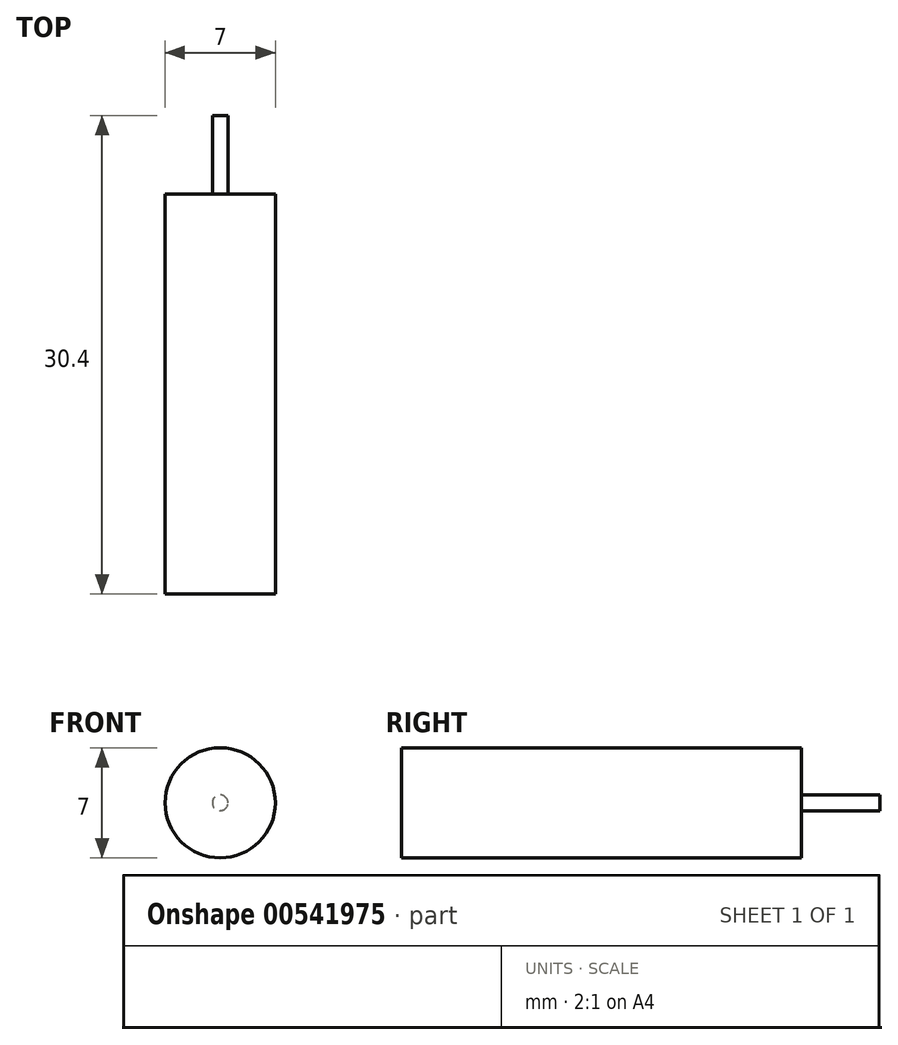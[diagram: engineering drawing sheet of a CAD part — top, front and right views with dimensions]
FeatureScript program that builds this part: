
annotation { "Feature Type Name" : "Feature", "Feature Type Description" : "" }
export const myFeature = defineFeature(function(context is Context, id is Id, definition is map)
    precondition{}
    {
        {
            var Q0;
            Q0=qCreatedBy(makeId("Front.planeOp"),FACE);
            var sketch = newSketch(context, id + "F0", { "sketchPlane" : qUnion([Q0])});
            skCircle(sketch, "E0", {"center": v(0, 0) * mm, "radius": 3.5 * mm});
            skSolve(sketch);
        }
        {
            var Q0;
            Q0 = qSketchRegion(id + "F0", true);
            var sketch = newSketch(context, id + "F1", { "sketchPlane" : qUnion([Q0])});
            skSolve(sketch);
        }
        {
            var Q0;
            Q0 = qSketchRegion(id + "F1", true);
            var Q1;
            Q1=makeQuery(id+"F1.imprint","IMPRINT",FACE,{"disambiguationData":[TD([[makeQuery(id+"F1.imprint","IMPRINT",EDGE,{"derivedFrom":makeQuery(id+"F0.imprint","IMPRINT",EDGE,{"derivedFrom":sQuery(id+"F0.wireOp",EDGE,"E0")})}),1.0]])]});
            extrude(context, id + "F2", {"entities" : qUnion([Q0, Q1]), "depth" : 15 * mm, "offsetDistance" : 25.4 * mm});
        }
        {
            var Q0;
            Q0 = qSketchRegion(id + "F0", true);
            var sketch = newSketch(context, id + "F3", { "sketchPlane" : qUnion([Q0])});
            skCircle(sketch, "E1", {"center": v(0, 0) * mm, "radius": 0.5 * mm});
            skSolve(sketch);
        }
        {
            var Q0;
            Q0 = qSketchRegion(id + "F3", true);
            extrude(context, id + "F4", {"entities" : qUnion([Q0]), "operationType" : NewBodyOperationType.ADD, "depth" : 5 * mm, "offsetDistance" : 25.4 * mm});
        }
        {
            var Q0;
            Q0 = qSketchRegion(id + "F0", true);
            extrude(context, id + "F5", {"entities" : qUnion([Q0]), "operationType" : NewBodyOperationType.ADD, "depth" : 25.4 * mm, "offsetDistance" : 25.4 * mm});
        }
        {
            var Q0;
            Q0=makeQuery(id+"F2.opExtrude","CAP_FACE",FACE,{"disambiguationData":[OSD([sQuery(id+"F0.wireOp",EDGE,"E0")])],"isStart":true});
            var sketch = newSketch(context, id + "F6", { "sketchPlane" : qUnion([Q0])});
            skCircle(sketch, "E2", {"center": v(0, 0) * mm, "radius": 0.5 * mm});
            skSolve(sketch);
        }
        {
            var Q0;
            Q0 = qSketchRegion(id + "F6", true);
            extrude(context, id + "F7", {"entities" : qUnion([Q0]), "operationType" : NewBodyOperationType.ADD, "depth" : 5 * mm, "offsetDistance" : 25.4 * mm});
        }
    });
